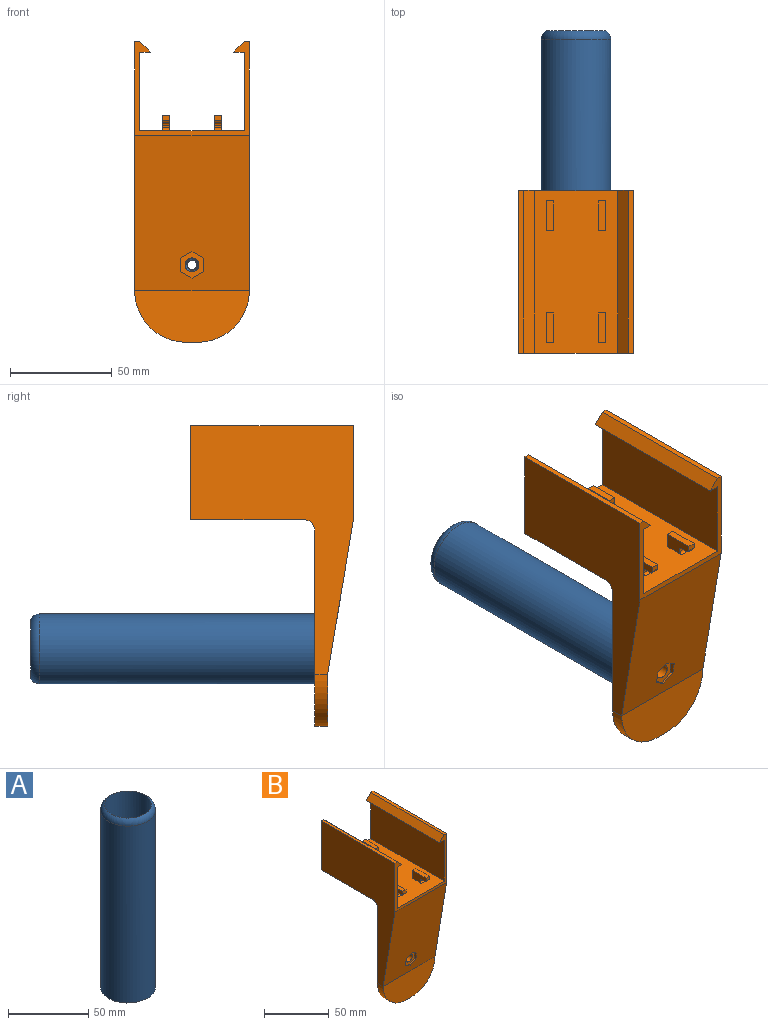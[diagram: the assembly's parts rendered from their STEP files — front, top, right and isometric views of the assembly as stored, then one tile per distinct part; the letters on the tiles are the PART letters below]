
ASSEMBLY  parts=2 mates=1
PART A: 12 faces, bbox 37.1x37.1x140.8 mm
  f0: cone r=3.43mm half-angle=45deg, axis (0,0,-1), area 16.2mm2, adj f1,f3,f6,f7,f8
  f1: cone r=3.43mm half-angle=45deg, axis (0,0,-1), area 1.6mm2, adj f0,f4,f7,f8
  f2: cone r=3.43mm half-angle=45deg, axis (0,0,1), area 18mm2, adj f3,f4,f5,f7,f8
  f3: cylinder r=3.17mm len=21.72mm, axis (0,0,-1), area 54.1mm2, adj f0,f2,f7,f8
  f4: cylinder r=2.35mm len=20.07mm, axis (0,0,1), area 37mm2, adj f1,f2,f7,f8
  f5: plane 29.21x29.21mm, normal (0,0,1), area 633.2mm2, adj f2,f9
  f6: plane 34.29x34.29mm, normal (0,0,-1), area 886.5mm2, adj f0,f10
  f7: bspline ~22.28x7.33mm, area 273mm2, adj f0,f1,f2,f3,f4
  f8: bspline ~22.49x7.33mm, area 273.4mm2, adj f0,f1,f2,f3,f4
  f9: cylinder r=14.61mm len=117.48mm, axis (0,0,-1), area 10780.2mm2, adj f5,f11
  f10: cylinder r=17.14mm len=135.3mm, axis (0,0,-1), area 14575.3mm2, adj f6,f11
  f11: torus R=12.06mm, axis (0,0,1), area 543.7mm2, adj f9,f10
PART B: 69 faces, bbox 56.4x80x147.8 mm
  f0: plane 76.2x56.39mm, normal (0,-0.99,-0.16), area 4243.9mm2, adj f2,f6,f38,f40,f62,f63,f64,f65
  f1: cylinder r=3.43mm len=6.86mm, axis (0,1,0), area 136.8mm2, adj f45,f68
  f2: plane 56.39x46.23mm, normal (0,-1,0), area 391mm2, adj f0,f3,f4,f12,f37,f38,f39,f40
  f3: plane 80.01x2.54mm, normal (0,0,1), area 203.2mm2, adj f2,f5,f38,f61
  f4: plane 80.01x2.54mm, normal (0,0,1), area 203.2mm2, adj f2,f5,f40,f60
  f5: plane 56.39x46.23mm, normal (0,1,0), area 391mm2, adj f3,f4,f7,f12,f37,f38,f39,f40
  f6: plane 56.39x25.4mm, normal (0,-1,0), area 1155.4mm2, adj f0,f46,f47,f48
  f7: plane 56.39x55.88mm, normal (0,0,-1), area 3151mm2, adj f5,f38,f40,f49
  f8: plane 3.56x2.54mm, normal (0,-1,0), area 9mm2, adj f9,f13,f14,f41
  f9: plane 14.73x7.62mm, normal (-1,0,0), area 88.4mm2, adj f8,f12,f13,f15,f35,f36,f41,f50
  f10: plane 3.56x2.54mm, normal (0,-1,0), area 9mm2, adj f11,f16,f17,f42
  f11: plane 14.73x7.62mm, normal (-1,0,0), area 88.4mm2, adj f10,f12,f16,f18,f33,f34,f42,f52
  f12: plane 80.01x51.31mm, normal (0,0,1), area 3967.9mm2, adj f2,f5,f9,f11,f14,f15,f17,f18
  f13: plane 14.73x3.56mm, normal (0,0,1), area 52.4mm2, adj f8,f9,f14,f15
  f14: plane 14.73x7.62mm, normal (1,0,0), area 88.4mm2, adj f8,f12,f13,f15,f35,f36,f41,f50
  f15: plane 7.62x3.56mm, normal (0,1,0), area 27.1mm2, adj f9,f12,f13,f14
  f16: plane 14.73x3.56mm, normal (0,0,1), area 52.4mm2, adj f10,f11,f17,f18
  f17: plane 14.73x7.62mm, normal (1,0,0), area 88.4mm2, adj f10,f12,f16,f18,f33,f34,f42,f52
  f18: plane 7.62x3.56mm, normal (0,1,0), area 27.1mm2, adj f11,f12,f16,f17
  f19: plane 14.73x3.56mm, normal (0,0,1), area 52.4mm2, adj f20,f21,f22,f23
  f20: plane 14.73x7.62mm, normal (1,0,0), area 88.4mm2, adj f12,f19,f21,f23,f31,f32,f43,f54
  f21: plane 3.56x2.54mm, normal (0,-1,0), area 9mm2, adj f19,f20,f22,f43
  f22: plane 14.73x7.62mm, normal (-1,0,0), area 88.4mm2, adj f12,f19,f21,f23,f31,f32,f43,f54
  f23: plane 7.62x3.56mm, normal (0,1,0), area 27.1mm2, adj f12,f19,f20,f22
  f24: plane 14.73x3.56mm, normal (0,0,1), area 52.4mm2, adj f25,f26,f27,f28
  f25: plane 3.56x2.54mm, normal (0,-1,0), area 9mm2, adj f24,f26,f28,f44
  f26: plane 14.73x7.62mm, normal (-1,0,0), area 88.4mm2, adj f12,f24,f25,f27,f29,f30,f44,f56
  f27: plane 7.62x3.56mm, normal (0,1,0), area 27.1mm2, adj f12,f24,f26,f28
  f28: plane 14.73x7.62mm, normal (1,0,0), area 88.4mm2, adj f12,f24,f25,f27,f29,f30,f44,f56
  f29: plane 3.56x1.27mm, normal (0,-1,0), area 4.5mm2, adj f26,f28,f56,f57
  f30: plane 3.81x3.56mm, normal (0,0,-1), area 13.5mm2, adj f26,f28,f44,f56
  f31: plane 3.56x1.27mm, normal (0,-1,0), area 4.5mm2, adj f20,f22,f54,f55
  f32: plane 3.81x3.56mm, normal (0,0,-1), area 13.5mm2, adj f20,f22,f43,f54
  f33: plane 3.81x3.56mm, normal (0,0,-1), area 13.5mm2, adj f11,f17,f42,f53
  f34: plane 3.56x1.27mm, normal (0,-1,0), area 4.5mm2, adj f11,f17,f52,f53
  f35: plane 3.81x3.56mm, normal (0,0,-1), area 13.5mm2, adj f9,f14,f41,f51
  f36: plane 3.56x1.27mm, normal (0,-1,0), area 4.5mm2, adj f9,f14,f50,f51
  f37: plane 80.01x38.61mm, normal (1,0,0), area 3089mm2, adj f2,f5,f12,f58
  f38: plane 122.43x80.01mm, normal (-1,0,0), area 4672mm2, adj f0,f2,f3,f5,f7,f45,f47,f49
  f39: plane 80.01x38.61mm, normal (-1,0,0), area 3089mm2, adj f2,f5,f12,f59
  f40: plane 122.43x80.01mm, normal (1,0,0), area 4672mm2, adj f0,f2,f4,f5,f7,f45,f48,f49
  f41: cylinder r=1.27mm len=3.56mm, axis (-1,0,0), area 7.1mm2, adj f8,f9,f14,f35
  f42: cylinder r=1.27mm len=3.56mm, axis (-1,0,0), area 7.1mm2, adj f10,f11,f17,f33
  f43: cylinder r=1.27mm len=3.56mm, axis (1,0,0), area 7.1mm2, adj f20,f21,f22,f32
  f44: cylinder r=1.27mm len=3.56mm, axis (1,0,0), area 7.1mm2, adj f25,f26,f28,f30
  f45: plane 96.52x56.39mm, normal (0,1,0), area 5128.7mm2, adj f1,f38,f40,f46,f47,f48,f49
  f46: plane 6.35x5.59mm, normal (0,0,-1), area 35.5mm2, adj f6,f45,f47,f48
  f47: cylinder r=25.4mm len=25.4mm, axis (0,-1,0), area 253.4mm2, adj f6,f38,f45,f46
  f48: cylinder r=25.4mm len=25.4mm, axis (0,-1,0), area 253.4mm2, adj f6,f40,f45,f46
  f49: cylinder r=5.08mm len=56.39mm, axis (-1,0,0), area 450mm2, adj f7,f38,f40,f45
  f50: cylinder r=1.27mm len=3.56mm, axis (1,0,0), area 7.1mm2, adj f9,f12,f14,f36
  f51: cylinder r=1.27mm len=3.56mm, axis (-1,0,0), area 7.1mm2, adj f9,f14,f35,f36
  f52: cylinder r=1.27mm len=3.56mm, axis (1,0,0), area 7.1mm2, adj f11,f12,f17,f34
  f53: cylinder r=1.27mm len=3.56mm, axis (-1,0,0), area 7.1mm2, adj f11,f17,f33,f34
  f54: cylinder r=1.27mm len=3.56mm, axis (-1,0,0), area 7.1mm2, adj f20,f22,f31,f32
  f55: cylinder r=1.27mm len=3.56mm, axis (1,0,0), area 7.1mm2, adj f12,f20,f22,f31
  f56: cylinder r=1.27mm len=3.56mm, axis (-1,0,0), area 7.1mm2, adj f26,f28,f29,f30
  f57: cylinder r=1.27mm len=3.56mm, axis (1,0,0), area 7.1mm2, adj f12,f26,f28,f29
  f58: plane 80.01x5.08mm, normal (0,0,-1), area 406.5mm2, adj f2,f5,f37,f61
  f59: plane 80.01x5.08mm, normal (0,0,-1), area 406.5mm2, adj f2,f5,f39,f60
  f60: plane 80.01x5.08mm, normal (-0.71,0,0.71), area 574.8mm2, adj f2,f4,f5,f59
  f61: plane 80.01x5.08mm, normal (0.71,0,0.71), area 574.8mm2, adj f2,f3,f5,f58
  f62: plane 5.65x3.26mm, normal (-0.5,0,-0.87), area 19.1mm2, adj f0,f63,f65,f68
  f63: plane 5.65x3.26mm, normal (0.5,0,-0.87), area 19.1mm2, adj f0,f62,f64,f68
  f64: plane 6.53x2.66mm, normal (1,0,0), area 13.8mm2, adj f0,f63,f66,f68
  f65: plane 6.53x2.66mm, normal (-1,0,0), area 13.8mm2, adj f0,f62,f67,f68
  f66: plane 5.65x3.26mm, normal (0.5,0,0.87), area 8.5mm2, adj f0,f64,f67,f68
  f67: plane 5.65x3.26mm, normal (-0.5,0,0.87), area 8.5mm2, adj f0,f65,f66,f68
  f68: plane 13.05x11.3mm, normal (0,-1,0), area 73.7mm2, adj f1,f62,f63,f64,f65,f66,f67
PLACE A rot(axis=(-1,0,0),90deg) t=(-17.58,-25.11,-60.16)mm
PLACE B t=(-17.58,-15.58,3.34)mm fixed
MATE fastened A.f10 <-> B.f1  axis (0,-1,0) through (-17.58,-47.33,-60.16)mm
